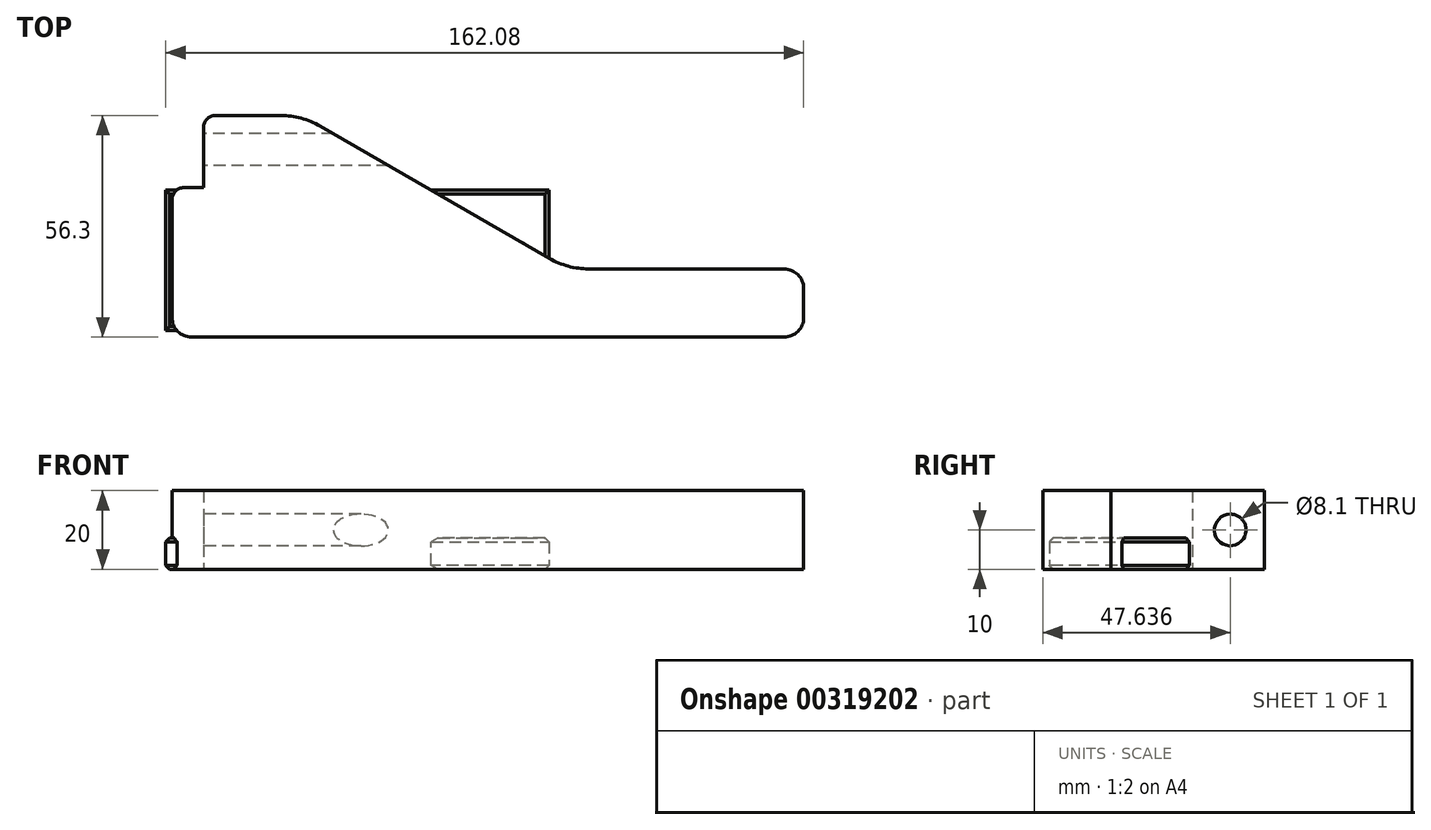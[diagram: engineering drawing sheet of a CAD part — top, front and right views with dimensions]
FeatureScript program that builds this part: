
annotation { "Feature Type Name" : "Feature", "Feature Type Description" : "" }
export const myFeature = defineFeature(function(context is Context, id is Id, definition is map)
    precondition{}
    {
        {
            var Q0;
            Q0=qCreatedBy(makeId("Top.planeOp"),FACE);
            var sketch = newSketch(context, id + "F0", { "sketchPlane" : qUnion([Q0])});
            skCircle(sketch, "E0", {"center": v(0, 0) * mm, "radius": 10.82 * mm});
            skLineSegment(sketch, "E1.bottom", {"start": v(-68.33, 17.82) * mm, "end": v(29.02, 17.82) * mm});
            skLineSegment(sketch, "E1.top", {"start": v(-68.33, -17.82) * mm, "end": v(29.02, -17.82) * mm});
            skLineSegment(sketch, "E1.left", {"start": v(-68.33, 17.82) * mm, "end": v(-68.33, -17.83) * mm});
            skLineSegment(sketch, "E1.right", {"start": v(29.02, 17.82) * mm, "end": v(29.02, -17.82) * mm});
            skCircle(sketch, "E2", {"center": v(19.92, 0) * mm, "radius": 4.1 * mm});
            skLineSegment(sketch, "E3.bottom", {"start": v(-61.32, 5.15) * mm, "end": v(-30.82, 5.15) * mm});
            skLineSegment(sketch, "E3.top", {"start": v(-61.32, -5.15) * mm, "end": v(-30.82, -5.15) * mm});
            skLineSegment(sketch, "E3.left", {"start": v(-61.32, 5.15) * mm, "end": v(-61.32, -5.15) * mm});
            skLineSegment(sketch, "E3.right", {"start": v(-30.82, 5.15) * mm, "end": v(-30.82, -5.15) * mm});
            skPoint(sketch, "E4", {"position": v(-30.82, 0) * mm});
            skSolve(sketch);
        }
        {
            var Q0;
            Q0 = qSketchRegion(id + "F0", true);
            extrude(context, id + "F1", {"entities" : qUnion([Q0]), "depth" : 8 * mm, "offsetDistance" : 25 * mm});
        }
        {
            var Q0;
            Q0=makeQuery(id+"F1.opExtrude","SWEPT_FACE",FACE,{"disambiguationData":[OSD([sQuery(id+"F0.wireOp",EDGE,"E1.top")])]});
            var sketch = newSketch(context, id + "F2", { "sketchPlane" : qUnion([Q0])});
            skCircle(sketch, "E5", {"center": v(0, 4) * mm, "radius": 1.55 * mm});
            skSolve(sketch);
        }
        {
            var Q0;
            Q0 = qSketchRegion(id + "F2", true);
            extrude(context, id + "F3", {"entities" : qUnion([Q0]), "operationType" : NewBodyOperationType.REMOVE, "oppositeDirection" : true, "depth" : 12 * mm, "offsetDistance" : 25 * mm});
        }
        {
            var Q0;
            Q0=makeQuery(id+"F1.opExtrude","CAP_FACE",FACE,{"disambiguationData":[OSD([sQuery(id+"F0.wireOp",EDGE,"E0"),sQuery(id+"F0.wireOp",EDGE,"E1.bottom"),sQuery(id+"F0.wireOp",EDGE,"E1.top"),sQuery(id+"F0.wireOp",EDGE,"E1.left"),sQuery(id+"F0.wireOp",EDGE,"E1.right"),sQuery(id+"F0.wireOp",EDGE,"E2"),sQuery(id+"F0.wireOp",EDGE,"E3.bottom"),sQuery(id+"F0.wireOp",EDGE,"E3.top"),sQuery(id+"F0.wireOp",EDGE,"E3.left"),sQuery(id+"F0.wireOp",EDGE,"E3.right")])],"isStart":false});
            var Q1;
            Q1=makeQuery(id+"F1.opExtrude","CAP_FACE",FACE,{"disambiguationData":[OSD([sQuery(id+"F0.wireOp",EDGE,"E0"),sQuery(id+"F0.wireOp",EDGE,"E1.bottom"),sQuery(id+"F0.wireOp",EDGE,"E1.top"),sQuery(id+"F0.wireOp",EDGE,"E1.left"),sQuery(id+"F0.wireOp",EDGE,"E1.right"),sQuery(id+"F0.wireOp",EDGE,"E2"),sQuery(id+"F0.wireOp",EDGE,"E3.bottom"),sQuery(id+"F0.wireOp",EDGE,"E3.top"),sQuery(id+"F0.wireOp",EDGE,"E3.left"),sQuery(id+"F0.wireOp",EDGE,"E3.right")])],"isStart":true});
            var Q2;
            Q2=makeQuery(id+"F3.boolean.opBoolean","COPY",EDGE,{"derivedFrom":makeQuery(id+"F3.opExtrude","CAP_EDGE",EDGE,{"disambiguationData":[OSD([sQuery(id+"F2.wireOp",EDGE,"E5")])],"isStart":true})});
            chamfer(context, id + "F4", {"entities" : qUnion([Q0, Q1, Q2]), "width" : 1 * mm, "tangentPropagation" : true});
        }
        {
            var Q0;
            Q0=qCreatedBy(makeId("Top.planeOp"),FACE);
            var sketch = newSketch(context, id + "F5", { "sketchPlane" : qUnion([Q0])});
            skLineSegment(sketch, "E6", {"start": v(-58.75, 36.8) * mm, "end": v(-58.75, 19.49) * mm});
            skLineSegment(sketch, "E7", {"start": v(-58.75, 19.49) * mm, "end": v(-33.75, 19.49) * mm});
            skLineSegment(sketch, "E8", {"start": v(-33.75, 19.49) * mm, "end": v(33.75, -19.49) * mm});
            skLineSegment(sketch, "E9", {"start": v(33.75, -19.49) * mm, "end": v(93.75, -19.49) * mm});
            skLineSegment(sketch, "E10", {"start": v(93.75, -19.49) * mm, "end": v(93.75, -2.17) * mm});
            skLineSegment(sketch, "E11", {"start": v(93.75, -2.17) * mm, "end": v(33.75, -2.17) * mm});
            skLineSegment(sketch, "E12", {"start": v(33.75, -2.17) * mm, "end": v(-33.75, 36.8) * mm});
            skLineSegment(sketch, "E13", {"start": v(-33.75, 36.8) * mm, "end": v(-58.75, 36.8) * mm});
            skPoint(sketch, "E14", {"position": v(0, 0) * mm});
            skSolve(sketch);
        }
        {
            var Q0;
            Q0 = qSketchRegion(id + "F5", true);
            extrude(context, id + "F6", {"entities" : qUnion([Q0]), "depth" : 20 * mm, "offsetDistance" : 25 * mm});
        }
        {
            var Q0;
            Q0=makeQuery(id+"F6.opExtrude","SWEPT_FACE",FACE,{"disambiguationData":[OSD([sQuery(id+"F5.wireOp",EDGE,"E6")])]});
            var sketch = newSketch(context, id + "F7", { "sketchPlane" : qUnion([Q0])});
            skLineSegment(sketch, "E15", {"start": v(-36.8, 20) * mm, "end": v(-19.49, 0) * mm, "construction": true});
            skCircle(sketch, "E16", {"center": v(-28.15, 10) * mm, "radius": 4.05 * mm});
            skSolve(sketch);
        }
        {
            var Q0;
            Q0 = qSketchRegion(id + "F7", true);
            extrude(context, id + "F8", {"entities" : qUnion([Q0]), "operationType" : NewBodyOperationType.REMOVE, "endBound" : BoundingType.THROUGH_ALL, "oppositeDirection" : true, "depth" : 25 * mm, "offsetDistance" : 25 * mm});
        }
        {
            var Q0;
            Q0=qCreatedBy(makeId("Top.planeOp"),FACE);
            var sketch = newSketch(context, id + "F9", { "sketchPlane" : qUnion([Q0])});
            skLineSegment(sketch, "E17.0.0", {"start": v(33.75, -2.17) * mm, "end": v(-33.75, 36.8) * mm, "construction": true});
            skLineSegment(sketch, "E17.0.1", {"start": v(-33.75, 36.8) * mm, "end": v(-58.75, 36.8) * mm, "construction": true});
            skLineSegment(sketch, "E17.0.2", {"start": v(-58.75, 36.8) * mm, "end": v(-58.75, 19.49) * mm, "construction": true});
            skLineSegment(sketch, "E17.0.3", {"start": v(-58.75, 19.49) * mm, "end": v(-33.75, 19.49) * mm});
            skLineSegment(sketch, "E17.0.4", {"start": v(-33.75, 19.49) * mm, "end": v(33.75, -19.49) * mm});
            skLineSegment(sketch, "E17.0.5", {"start": v(33.75, -19.49) * mm, "end": v(93.75, -19.49) * mm, "construction": true});
            skLineSegment(sketch, "E17.0.6", {"start": v(93.75, -19.49) * mm, "end": v(93.75, -2.17) * mm, "construction": true});
            skLineSegment(sketch, "E17.0.7", {"start": v(93.75, -2.17) * mm, "end": v(33.75, -2.17) * mm, "construction": true});
            skLineSegment(sketch, "E18", {"start": v(-58.75, 19.49) * mm, "end": v(-58.75, 18.49) * mm});
            skLineSegment(sketch, "E19", {"start": v(-58.75, 18.49) * mm, "end": v(-66.75, 18.49) * mm});
            skLineSegment(sketch, "E20", {"start": v(-66.75, 18.49) * mm, "end": v(-66.75, -19.49) * mm});
            skLineSegment(sketch, "E21", {"start": v(-66.75, -19.49) * mm, "end": v(33.75, -19.49) * mm});
            skSolve(sketch);
        }
        {
            var Q0;
            Q0=makeQuery(id+"F9.imprint","IMPRINT",FACE,{"disambiguationData":[TD([[makeQuery(id+"F9.imprint","IMPRINT",EDGE,{"derivedFrom":sQuery(id+"F9.wireOp",EDGE,"E17.0.3")}),-1.0]])]});
            var Q1;
            Q1 = qConstructionFilter(qBodyType(qCreatedBy(id + "F9" ,EDGE), BodyType.WIRE), ConstructionObject.NO);
            extrude(context, id + "F10", {"entities" : qUnion([Q0]), "operationType" : NewBodyOperationType.ADD, "surfaceEntities" : qUnion([Q1]), "depth" : 20 * mm, "offsetDistance" : 25 * mm});
        }
        {
            var Q0;
            Q0=makeQuery(id+"F6.opExtrude","SWEPT_EDGE",EDGE,{"disambiguationData":[OSD([sQuery(id+"F5.wireOp",EDGE,"E12"),sQuery(id+"F5.wireOp",EDGE,"E13")])]});
            var Q1;
            Q1=makeQuery(id+"F6.opExtrude","SWEPT_EDGE",EDGE,{"disambiguationData":[OSD([sQuery(id+"F5.wireOp",EDGE,"E11"),sQuery(id+"F5.wireOp",EDGE,"E12")])]});
            fillet(context, id + "F11", {"entities" : qUnion([Q0, Q1]), "radius" : 20 * mm, "tangentPropagation" : true, "allowEdgeOverflow" : false});
        }
        {
            var Q0;
            Q0=makeQuery(id+"F6.opExtrude","SWEPT_EDGE",EDGE,{"disambiguationData":[OSD([sQuery(id+"F5.wireOp",EDGE,"E10"),sQuery(id+"F5.wireOp",EDGE,"E11")])]});
            var Q1;
            Q1=makeQuery(id+"F6.opExtrude","SWEPT_EDGE",EDGE,{"disambiguationData":[OSD([sQuery(id+"F5.wireOp",EDGE,"E9"),sQuery(id+"F5.wireOp",EDGE,"E10")])]});
            var Q2;
            Q2=makeQuery(id+"F10.opExtrude","SWEPT_EDGE",EDGE,{"disambiguationData":[OSD([sQuery(id+"F9.wireOp",EDGE,"E20"),sQuery(id+"F9.wireOp",EDGE,"E21")])]});
            fillet(context, id + "F12", {"entities" : qUnion([Q0, Q1, Q2]), "radius" : 5 * mm, "tangentPropagation" : true, "allowEdgeOverflow" : false});
        }
        {
            var Q0;
            Q0=makeQuery(id+"F10.opExtrude","SWEPT_EDGE",EDGE,{"disambiguationData":[OSD([sQuery(id+"F9.wireOp",EDGE,"E19"),sQuery(id+"F9.wireOp",EDGE,"E20")])]});
            var Q1;
            Q1=makeQuery(id+"F6.opExtrude","SWEPT_EDGE",EDGE,{"disambiguationData":[OSD([sQuery(id+"F5.wireOp",EDGE,"E6"),sQuery(id+"F5.wireOp",EDGE,"E13")])]});
            fillet(context, id + "F13", {"entities" : qUnion([Q0, Q1]), "radius" : 3 * mm, "tangentPropagation" : true, "allowEdgeOverflow" : false});
        }
    });
